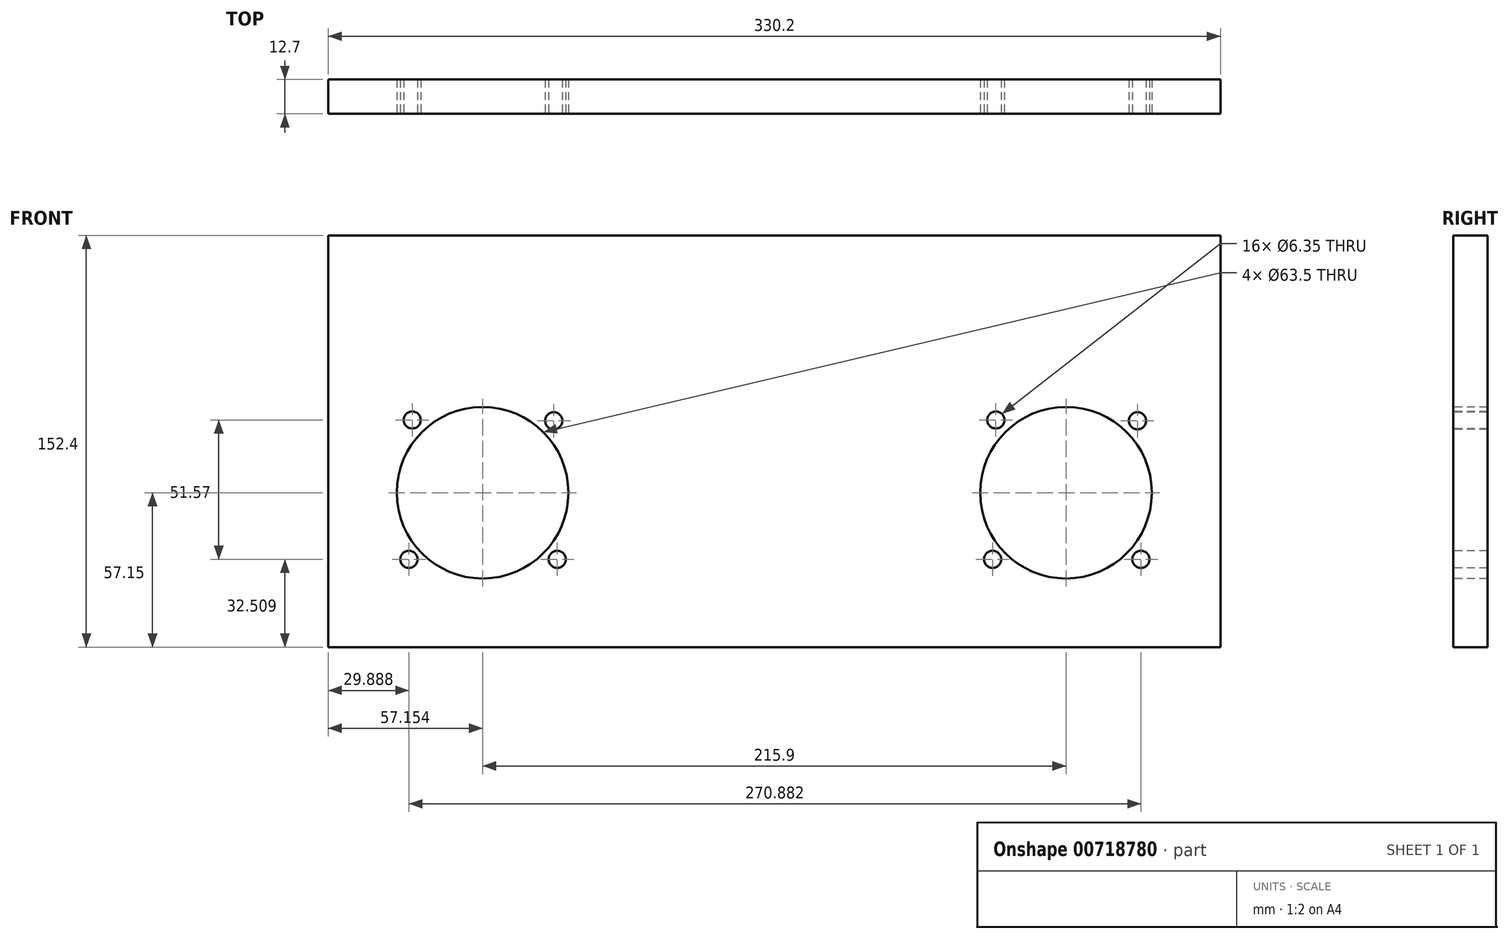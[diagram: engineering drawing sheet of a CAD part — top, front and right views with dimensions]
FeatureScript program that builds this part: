
annotation { "Feature Type Name" : "Feature", "Feature Type Description" : "" }
export const myFeature = defineFeature(function(context is Context, id is Id, definition is map)
    precondition{}
    {
        {
            var Q0;
            Q0=qCreatedBy(makeId("Front.planeOp"),FACE);
            var sketch = newSketch(context, id + "F0", { "sketchPlane" : qUnion([Q0])});
            skLineSegment(sketch, "E0.bottom", {"start": v(-159.69, 59.82) * mm, "end": v(170.51, 59.82) * mm});
            skLineSegment(sketch, "E0.top", {"start": v(-159.69, -92.58) * mm, "end": v(170.51, -92.58) * mm});
            skLineSegment(sketch, "E0.left", {"start": v(-159.69, 59.82) * mm, "end": v(-159.69, -92.58) * mm});
            skLineSegment(sketch, "E0.right", {"start": v(170.51, 59.82) * mm, "end": v(170.51, -92.58) * mm});
            skSolve(sketch);
        }
        {
            var Q0;
            Q0=makeQuery(id+"F0.imprint","IMPRINT",FACE,{"disambiguationData":[TD([[makeQuery(id+"F0.imprint","IMPRINT",EDGE,{"derivedFrom":sQuery(id+"F0.wireOp",EDGE,"E0.bottom")}),-1.0]])]});
            extrude(context, id + "F1", {"entities" : qUnion([Q0]), "depth" : 12.7 * mm, "offsetDistance" : 25.4 * mm});
        }
        {
            var Q0;
            Q0=makeQuery(id+"F1.opExtrude","CAP_FACE",FACE,{"disambiguationData":[OSD([sQuery(id+"F0.wireOp",EDGE,"E0.bottom"),sQuery(id+"F0.wireOp",EDGE,"E0.top"),sQuery(id+"F0.wireOp",EDGE,"E0.left"),sQuery(id+"F0.wireOp",EDGE,"E0.right")])],"isStart":false});
            var sketch = newSketch(context, id + "F2", { "sketchPlane" : qUnion([Q0])});
            skLineSegment(sketch, "E1.bottom", {"start": v(-134.29, -3.68) * mm, "end": v(-70.79, -3.68) * mm});
            skLineSegment(sketch, "E1.top", {"start": v(-134.29, -67.18) * mm, "end": v(-70.79, -67.18) * mm});
            skLineSegment(sketch, "E1.left", {"start": v(-134.29, -3.68) * mm, "end": v(-134.29, -67.18) * mm});
            skLineSegment(sketch, "E1.right", {"start": v(-70.79, -3.68) * mm, "end": v(-70.79, -67.18) * mm});
            skLineSegment(sketch, "E2.bottom", {"start": v(145.11, -67.18) * mm, "end": v(81.61, -67.18) * mm});
            skLineSegment(sketch, "E2.top", {"start": v(145.11, -3.68) * mm, "end": v(81.61, -3.68) * mm});
            skLineSegment(sketch, "E2.left", {"start": v(145.11, -67.18) * mm, "end": v(145.11, -3.68) * mm});
            skLineSegment(sketch, "E2.right", {"start": v(81.61, -67.18) * mm, "end": v(81.61, -3.68) * mm});
            skCircle(sketch, "E3", {"center": v(-102.54, -35.43) * mm, "radius": 31.75 * mm});
            skPoint(sketch, "E3.centerSnap0", {"position": v(-134.29, -35.43) * mm});
            skPoint(sketch, "E3.centerSnap1", {"position": v(-102.54, -3.68) * mm});
            skCircle(sketch, "E4", {"center": v(113.36, -35.43) * mm, "radius": 31.75 * mm});
            skPoint(sketch, "E4.centerSnap0", {"position": v(113.36, -3.68) * mm});
            skPoint(sketch, "E4.centerSnap1", {"position": v(145.11, -35.43) * mm});
            skCircle(sketch, "E5", {"center": v(-128.58, -8.5) * mm, "radius": 3.18 * mm});
            skCircle(sketch, "E6", {"center": v(-76.2, -8.79) * mm, "radius": 3.18 * mm});
            skCircle(sketch, "E7", {"center": v(-129.8, -60.07) * mm, "radius": 3.18 * mm});
            skCircle(sketch, "E8", {"center": v(-74.9, -60.07) * mm, "radius": 3.18 * mm});
            skLineSegment(sketch, "E9", {"start": v(-102.54, -3.68) * mm, "end": v(-102.54, -35.43) * mm});
            skLineSegment(sketch, "E10", {"start": v(-102.54, -3.68) * mm, "end": v(-102.54, -67.18) * mm, "construction": true});
            skPoint(sketch, "E11.centerSnap0", {"position": v(81.7, -35.43) * mm});
            skPoint(sketch, "E11.centerSnap1", {"position": v(113.45, -3.68) * mm});
            skCircle(sketch, "E12", {"center": v(87.4, -8.5) * mm, "radius": 3.18 * mm});
            skCircle(sketch, "E13", {"center": v(139.8, -8.79) * mm, "radius": 3.18 * mm});
            skCircle(sketch, "E14", {"center": v(86.18, -60.07) * mm, "radius": 3.18 * mm});
            skCircle(sketch, "E15", {"center": v(141.08, -60.07) * mm, "radius": 3.18 * mm});
            skLineSegment(sketch, "E16", {"start": v(113.45, -3.68) * mm, "end": v(113.45, -35.43) * mm});
            skLineSegment(sketch, "E17", {"start": v(113.45, -3.68) * mm, "end": v(113.45, -67.18) * mm, "construction": true});
            skSolve(sketch);
        }
        {
            var Q0;
            {var subQ0=sQuery(id+"F2.wireOp",EDGE,"E3");var subQ1=makeQuery(id+"F2.imprint","INTERSECT",VERTEX,{"derivedFrom":[sQuery(id+"F2.wireOp",EDGE,"E1.bottom"),subQ0]});Q0=makeQuery(id+"F2.imprint","IMPRINT",FACE,{"disambiguationData":[TD([[makeQuery(id+"F2.imprint","IMPRINT",EDGE,{"disambiguationData":[TD([[subQ1,1.0]])],"derivedFrom":subQ0}),1.0]])]});}
            var Q1;
            {var subQ0=sQuery(id+"F2.wireOp",EDGE,"E4");var subQ1=makeQuery(id+"F2.imprint","INTERSECT",VERTEX,{"derivedFrom":[sQuery(id+"F2.wireOp",EDGE,"E2.top"),subQ0]});Q1=makeQuery(id+"F2.imprint","IMPRINT",FACE,{"disambiguationData":[TD([[makeQuery(id+"F2.imprint","IMPRINT",EDGE,{"disambiguationData":[TD([[subQ1,1.0]])],"derivedFrom":subQ0}),1.0]])]});}
            var Q2;
            Q2=makeQuery(id+"F2.imprint","IMPRINT",FACE,{"disambiguationData":[TD([[makeQuery(id+"F2.imprint","IMPRINT",EDGE,{"derivedFrom":sQuery(id+"F2.wireOp",EDGE,"E6")}),1.0]])]});
            var Q3;
            Q3=makeQuery(id+"F2.imprint","IMPRINT",FACE,{"disambiguationData":[TD([[makeQuery(id+"F2.imprint","IMPRINT",EDGE,{"derivedFrom":sQuery(id+"F2.wireOp",EDGE,"E5")}),1.0]])]});
            var Q4;
            Q4=makeQuery(id+"F2.imprint","IMPRINT",FACE,{"disambiguationData":[TD([[makeQuery(id+"F2.imprint","IMPRINT",EDGE,{"derivedFrom":sQuery(id+"F2.wireOp",EDGE,"E7")}),1.0]])]});
            var Q5;
            Q5=makeQuery(id+"F2.imprint","IMPRINT",FACE,{"disambiguationData":[TD([[makeQuery(id+"F2.imprint","IMPRINT",EDGE,{"derivedFrom":sQuery(id+"F2.wireOp",EDGE,"E8")}),1.0]])]});
            var Q6;
            Q6=makeQuery(id+"F2.imprint","IMPRINT",FACE,{"disambiguationData":[TD([[makeQuery(id+"F2.imprint","IMPRINT",EDGE,{"derivedFrom":sQuery(id+"F2.wireOp",EDGE,"E12")}),1.0]])]});
            var Q7;
            Q7=makeQuery(id+"F2.imprint","IMPRINT",FACE,{"disambiguationData":[TD([[makeQuery(id+"F2.imprint","IMPRINT",EDGE,{"derivedFrom":sQuery(id+"F2.wireOp",EDGE,"E13")}),1.0]])]});
            var Q8;
            Q8=makeQuery(id+"F2.imprint","IMPRINT",FACE,{"disambiguationData":[TD([[makeQuery(id+"F2.imprint","IMPRINT",EDGE,{"derivedFrom":sQuery(id+"F2.wireOp",EDGE,"E15")}),1.0]])]});
            var Q9;
            Q9=makeQuery(id+"F2.imprint","IMPRINT",FACE,{"disambiguationData":[TD([[makeQuery(id+"F2.imprint","IMPRINT",EDGE,{"derivedFrom":sQuery(id+"F2.wireOp",EDGE,"E14")}),1.0]])]});
            extrude(context, id + "F3", {"entities" : qUnion([Q0, Q1, Q2, Q3, Q4, Q5, Q6, Q7, Q8, Q9]), "operationType" : NewBodyOperationType.REMOVE, "oppositeDirection" : true, "depth" : 25.4 * mm, "offsetDistance" : 25.4 * mm});
        }
    });
